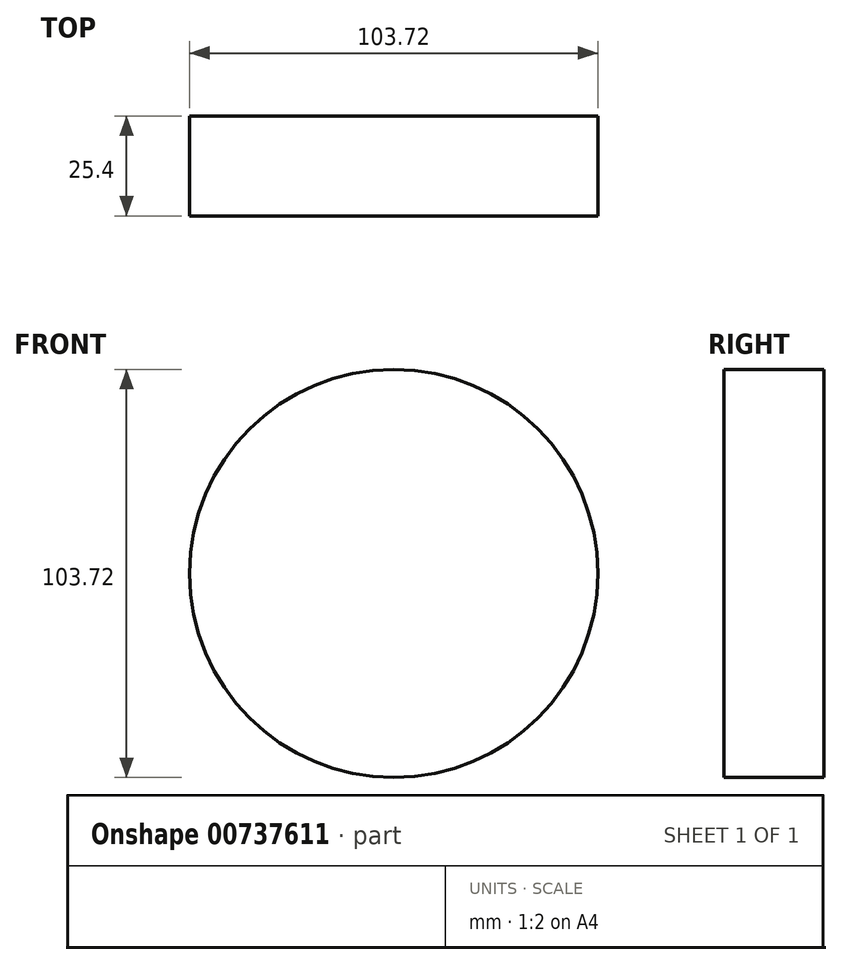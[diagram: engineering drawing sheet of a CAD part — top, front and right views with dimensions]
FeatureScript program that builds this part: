
annotation { "Feature Type Name" : "Feature", "Feature Type Description" : "" }
export const myFeature = defineFeature(function(context is Context, id is Id, definition is map)
    precondition{}
    {
        {
            var Q0;
            Q0=qCreatedBy(makeId("Front.planeOp"),FACE);
            var sketch = newSketch(context, id + "F0", { "sketchPlane" : qUnion([Q0])});
            skCircle(sketch, "E0", {"center": v(0, 0) * mm, "radius": 51.86 * mm});
            skSolve(sketch);
        }
        {
            var Q0;
            Q0 = qSketchRegion(id + "F0", true);
            extrude(context, id + "F1", {"entities" : qUnion([Q0]), "depth" : 25.4 * mm, "offsetDistance" : 25.4 * mm});
        }
    });
